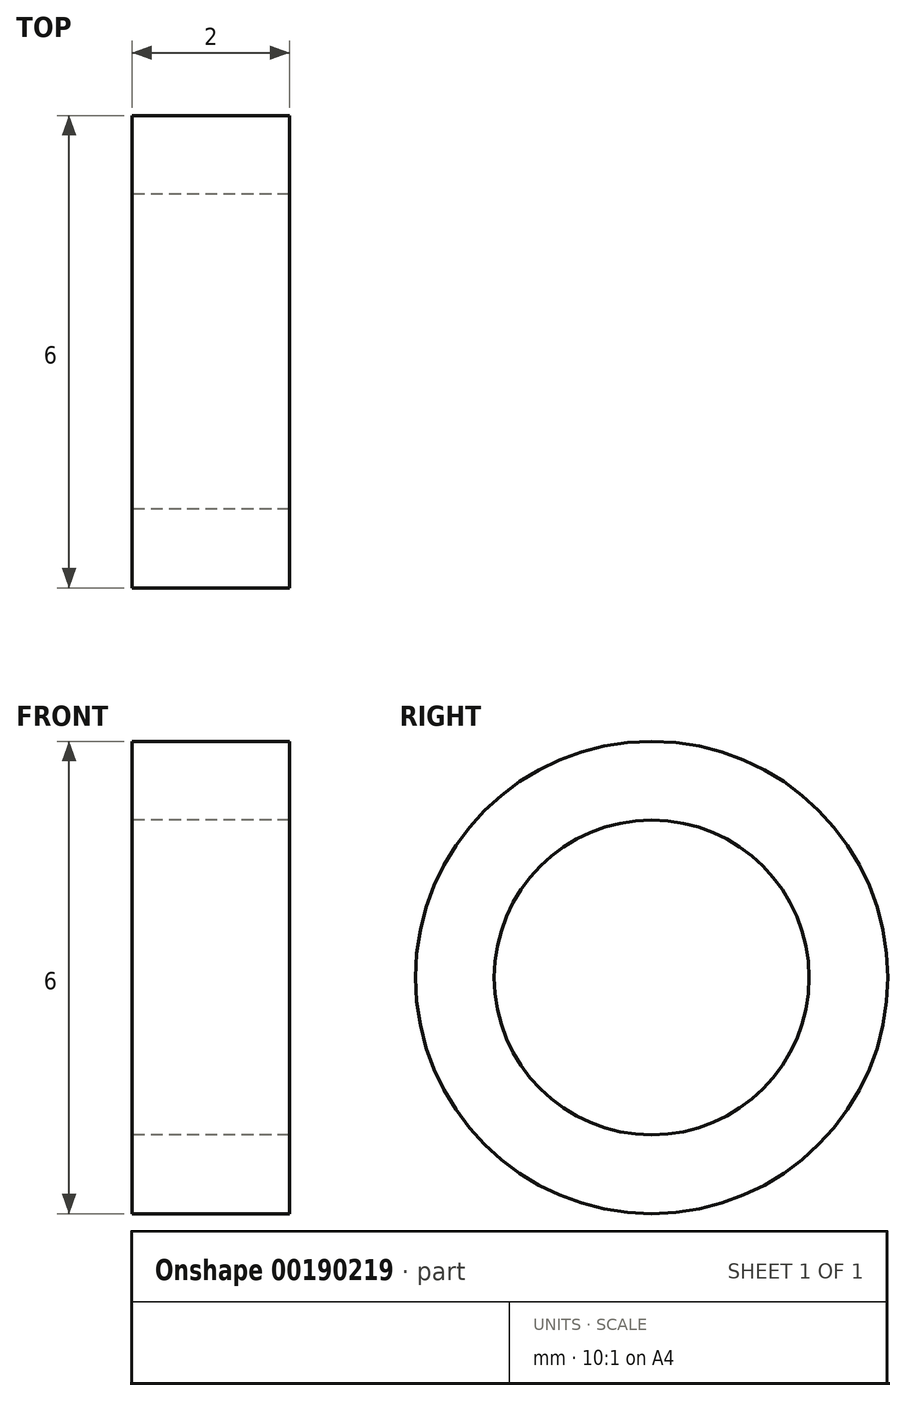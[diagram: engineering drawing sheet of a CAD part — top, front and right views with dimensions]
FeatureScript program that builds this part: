
annotation { "Feature Type Name" : "Feature", "Feature Type Description" : "" }
export const myFeature = defineFeature(function(context is Context, id is Id, definition is map)
    precondition{}
    {
        {
            var Q0;
            Q0=qCreatedBy(makeId("Right.planeOp"),FACE);
            var sketch = newSketch(context, id + "F0", { "sketchPlane" : qUnion([Q0])});
            skCircle(sketch, "E0", {"center": v(0, 0) * mm, "radius": 3 * mm});
            skCircle(sketch, "E1", {"center": v(0, 0) * mm, "radius": 2 * mm});
            skSolve(sketch);
        }
        {
            var Q0;
            Q0 = qSketchRegion(id + "F0", true);
            extrude(context, id + "F1", {"entities" : qUnion([Q0]), "depth" : 2 * mm});
        }
    });
